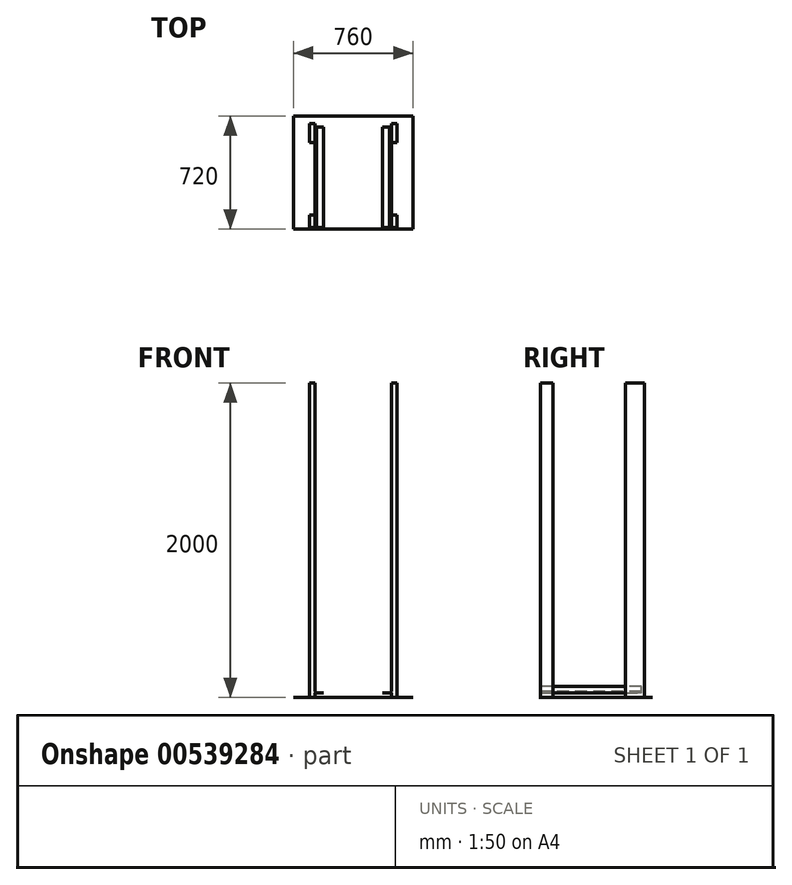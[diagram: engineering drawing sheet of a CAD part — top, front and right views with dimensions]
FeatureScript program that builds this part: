
annotation { "Feature Type Name" : "Feature", "Feature Type Description" : "" }
export const myFeature = defineFeature(function(context is Context, id is Id, definition is map)
    precondition{}
    {
        {
            var Q0;
            Q0=qCreatedBy(makeId("Top.planeOp"),FACE);
            var sketch = newSketch(context, id + "F0", { "sketchPlane" : qUnion([Q0])});
            skLineSegment(sketch, "E0.bottom", {"start": v(-380, 360) * mm, "end": v(380, 360) * mm});
            skLineSegment(sketch, "E0.top", {"start": v(-380, -360) * mm, "end": v(380, -360) * mm});
            skLineSegment(sketch, "E0.left", {"start": v(-380, 360) * mm, "end": v(-380, -360) * mm});
            skLineSegment(sketch, "E0.right", {"start": v(380, 360) * mm, "end": v(380, -360) * mm});
            skPoint(sketch, "E0.middle", {"position": v(0, 0) * mm});
            skLineSegment(sketch, "E1", {"start": v(0, -360) * mm, "end": v(0, -350) * mm});
            skLineSegment(sketch, "E2", {"start": v(0, -350) * mm, "end": v(243, -350) * mm});
            skLineSegment(sketch, "E3.bottom", {"start": v(243, -350) * mm, "end": v(278, -350) * mm});
            skLineSegment(sketch, "E3.top", {"start": v(243, -270) * mm, "end": v(278, -270) * mm});
            skLineSegment(sketch, "E3.left", {"start": v(243, -350) * mm, "end": v(243, -270) * mm});
            skLineSegment(sketch, "E3.right", {"start": v(278, -350) * mm, "end": v(278, -270) * mm});
            skLineSegment(sketch, "E4", {"start": v(243, -270) * mm, "end": v(243, 190) * mm});
            skLineSegment(sketch, "E5.bottom", {"start": v(243, 190) * mm, "end": v(278, 190) * mm});
            skLineSegment(sketch, "E5.top", {"start": v(243, 310) * mm, "end": v(278, 310) * mm});
            skLineSegment(sketch, "E5.left", {"start": v(243, 190) * mm, "end": v(243, 310) * mm});
            skLineSegment(sketch, "E5.right", {"start": v(278, 190) * mm, "end": v(278, 310) * mm});
            skLineSegment(sketch, "E6.MirrorCS", {"start": v(-243, -270) * mm, "end": v(-278, -270) * mm});
            skLineSegment(sketch, "E7.MirrorCS", {"start": v(-243, -350) * mm, "end": v(-278, -350) * mm});
            skLineSegment(sketch, "E8.MirrorCS", {"start": v(-278, -350) * mm, "end": v(-278, -270) * mm});
            skLineSegment(sketch, "E9.MirrorCS", {"start": v(-243, 310) * mm, "end": v(-278, 310) * mm});
            skLineSegment(sketch, "E10.MirrorCS", {"start": v(0, -350) * mm, "end": v(-243, -350) * mm});
            skLineSegment(sketch, "E11.MirrorCS", {"start": v(-243, -350) * mm, "end": v(-243, -270) * mm});
            skLineSegment(sketch, "E12.MirrorCS", {"start": v(-243, 190) * mm, "end": v(-278, 190) * mm});
            skLineSegment(sketch, "E13.MirrorCS", {"start": v(-278, 190) * mm, "end": v(-278, 310) * mm});
            skLineSegment(sketch, "E14.MirrorCS", {"start": v(-243, -270) * mm, "end": v(-243, 190) * mm});
            skLineSegment(sketch, "E15.MirrorCS", {"start": v(-243, 190) * mm, "end": v(-243, 310) * mm});
            skSolve(sketch);
        }
        {
            var Q0;
            Q0=qCreatedBy(makeId("Front.planeOp"),FACE);
            cPlane(context, id + "F1", {"entities" : qUnion([Q0]), "cplaneType" : CPlaneType.OFFSET, "offset" : 350 * mm, "width" : 150 * mm, "height" : 150 * mm});
        }
        {
            var Q0;
            {var subQ7=sQuery(id+"F0.wireOp",EDGE,"E0.top");Q0=makeQuery(id+"F0.imprint","IMPRINT",FACE,{"disambiguationData":[TD([[makeQuery(id+"F0.imprint","IMPRINT",EDGE,{"derivedFrom":subQ7}),1.0]])]});}
            var Q1;
            {var subQ3=sQuery(id+"F0.wireOp",EDGE,"euF1G4G7-zLeF-H2Gb-AlfA-z7sgLU5M8cCe");Q1=makeQuery(id+"F0.imprint","IMPRINT",FACE,{"disambiguationData":[TD([[makeQuery(id+"F0.imprint","IMPRINT",EDGE,{"derivedFrom":subQ3}),1.0]])]});}
            var Q2;
            {var subQ3=sQuery(id+"F0.wireOp",EDGE,"euF1G4G7-zLeF-H2Gb-AlfA-z7sgLU5M8cCe");Q2=makeQuery(id+"F0.imprint","IMPRINT",FACE,{"disambiguationData":[TD([[makeQuery(id+"F0.imprint","IMPRINT",EDGE,{"derivedFrom":subQ3}),-1.0]])]});}
            var Q3;
            {var subQ0=sQuery(id+"F0.wireOp",EDGE,"bGO4djBt-VMuH-sKPz-gY4S-efjFLGcQopZA");Q3=makeQuery(id+"F0.imprint","IMPRINT",FACE,{"disambiguationData":[TD([[makeQuery(id+"F0.imprint","IMPRINT",EDGE,{"derivedFrom":subQ0}),1.0]])]});}
            extrude(context, id + "F2", {"entities" : qUnion([Q0, Q1, Q2, Q3]), "depth" : 1 * mm, "offsetDistance" : 25 * mm});
        }
        {
            var Q0;
            Q0=qCreatedBy(id+"F1.planeOp",FACE);
            var sketch = newSketch(context, id + "F3", { "sketchPlane" : qUnion([Q0])});
            skLineSegment(sketch, "E16", {"start": v(0, 0) * mm, "end": v(0, 30) * mm});
            skLineSegment(sketch, "E17", {"start": v(0, 30) * mm, "end": v(-187.5, 30) * mm});
            skLineSegment(sketch, "E18", {"start": v(0, 29) * mm, "end": v(0, 30) * mm});
            skLineSegment(sketch, "E19", {"start": v(-187.5, 29) * mm, "end": v(-187.5, 30) * mm});
            skLineSegment(sketch, "E20", {"start": v(-187.5, 30) * mm, "end": v(-232.5, 30) * mm});
            skLineSegment(sketch, "E21", {"start": v(-232.5, 30) * mm, "end": v(-242.5, 30) * mm});
            skLineSegment(sketch, "E22", {"start": v(-242.5, 30) * mm, "end": v(-242.5, 70) * mm});
            skLineSegment(sketch, "E23", {"start": v(-242.5, 70) * mm, "end": v(-243.5, 70) * mm});
            skLineSegment(sketch, "E24", {"start": v(-243.5, 70) * mm, "end": v(-243.5, 30) * mm});
            skLineSegment(sketch, "E25", {"start": v(-243.5, 30) * mm, "end": v(-243.5, 29) * mm});
            skLineSegment(sketch, "E26", {"start": v(-243.5, 29) * mm, "end": v(-187.5, 29) * mm});
            skLineSegment(sketch, "E27", {"start": v(-232.5, 30) * mm, "end": v(-242.5, 40) * mm});
            skLineSegment(sketch, "E28.MirrorCS", {"start": v(187.5, 29) * mm, "end": v(187.5, 30) * mm});
            skLineSegment(sketch, "E29.MirrorCS", {"start": v(243.5, 30) * mm, "end": v(243.5, 29) * mm});
            skLineSegment(sketch, "E30.MirrorCS", {"start": v(242.5, 70) * mm, "end": v(243.5, 70) * mm});
            skLineSegment(sketch, "E31.MirrorCS", {"start": v(232.5, 30) * mm, "end": v(242.5, 40) * mm});
            skLineSegment(sketch, "E32.MirrorCS", {"start": v(232.5, 30) * mm, "end": v(242.5, 30) * mm});
            skLineSegment(sketch, "E33.MirrorCS", {"start": v(187.5, 30) * mm, "end": v(232.5, 30) * mm});
            skLineSegment(sketch, "E34.MirrorCS", {"start": v(243.5, 29) * mm, "end": v(187.5, 29) * mm});
            skLineSegment(sketch, "E35.MirrorCS", {"start": v(243.5, 70) * mm, "end": v(243.5, 30) * mm});
            skLineSegment(sketch, "E36.MirrorCS", {"start": v(0, 30) * mm, "end": v(187.5, 30) * mm});
            skLineSegment(sketch, "E37.MirrorCS", {"start": v(242.5, 30) * mm, "end": v(242.5, 70) * mm});
            skSolve(sketch);
        }
        {
            var Q0;
            Q0=makeQuery(id+"F0.imprint","IMPRINT",FACE,{"disambiguationData":[TD([[makeQuery(id+"F0.imprint","IMPRINT",EDGE,{"derivedFrom":sQuery(id+"F0.wireOp",EDGE,"E9.MirrorCS")}),1.0]])]});
            var Q1;
            Q1=makeQuery(id+"F0.imprint","IMPRINT",FACE,{"disambiguationData":[TD([[makeQuery(id+"F0.imprint","IMPRINT",EDGE,{"derivedFrom":sQuery(id+"F0.wireOp",EDGE,"E6.MirrorCS")}),1.0]])]});
            var Q2;
            Q2=makeQuery(id+"F0.imprint","IMPRINT",FACE,{"disambiguationData":[TD([[makeQuery(id+"F0.imprint","IMPRINT",EDGE,{"derivedFrom":sQuery(id+"F0.wireOp",EDGE,"E3.bottom")}),1.0]])]});
            var Q3;
            Q3=makeQuery(id+"F0.imprint","IMPRINT",FACE,{"disambiguationData":[TD([[makeQuery(id+"F0.imprint","IMPRINT",EDGE,{"derivedFrom":sQuery(id+"F0.wireOp",EDGE,"E5.bottom")}),1.0]])]});
            extrude(context, id + "F4", {"entities" : qUnion([Q0, Q1, Q2, Q3]), "operationType" : NewBodyOperationType.ADD, "depth" : 2000 * mm, "offsetDistance" : 25 * mm});
        }
        {
            var Q0;
            Q0=makeQuery(id+"F3.imprint","IMPRINT",FACE,{"disambiguationData":[TD([[makeQuery(id+"F3.imprint","IMPRINT",EDGE,{"derivedFrom":sQuery(id+"F3.wireOp",EDGE,"E19")}),1.0]])]});
            var Q1;
            {var subQ0=sQuery(id+"F3.wireOp",EDGE,"E21");Q1=makeQuery(id+"F3.imprint","IMPRINT",FACE,{"disambiguationData":[TD([[makeQuery(id+"F3.imprint","IMPRINT",EDGE,{"derivedFrom":subQ0}),-1.0]])]});}
            var Q2;
            {var subQ0=sQuery(id+"F3.wireOp",EDGE,"E31.MirrorCS");Q2=makeQuery(id+"F3.imprint","IMPRINT",FACE,{"disambiguationData":[TD([[makeQuery(id+"F3.imprint","IMPRINT",EDGE,{"derivedFrom":subQ0}),-1.0]])]});}
            var Q3;
            Q3=makeQuery(id+"F3.imprint","IMPRINT",FACE,{"disambiguationData":[TD([[makeQuery(id+"F3.imprint","IMPRINT",EDGE,{"derivedFrom":sQuery(id+"F3.wireOp",EDGE,"E28.MirrorCS")}),-1.0]])]});
            extrude(context, id + "F5", {"entities" : qUnion([Q0, Q1, Q2, Q3]), "operationType" : NewBodyOperationType.ADD, "oppositeDirection" : true, "depth" : 640 * mm, "offsetDistance" : 25 * mm});
        }
        {
            var Q0;
            Q0=qCreatedBy(makeId("Top.planeOp"),FACE);
            cPlane(context, id + "F6", {"entities" : qUnion([Q0]), "cplaneType" : CPlaneType.OFFSET, "offset" : 30 * mm, "width" : 150 * mm, "height" : 150 * mm});
        }
    });
